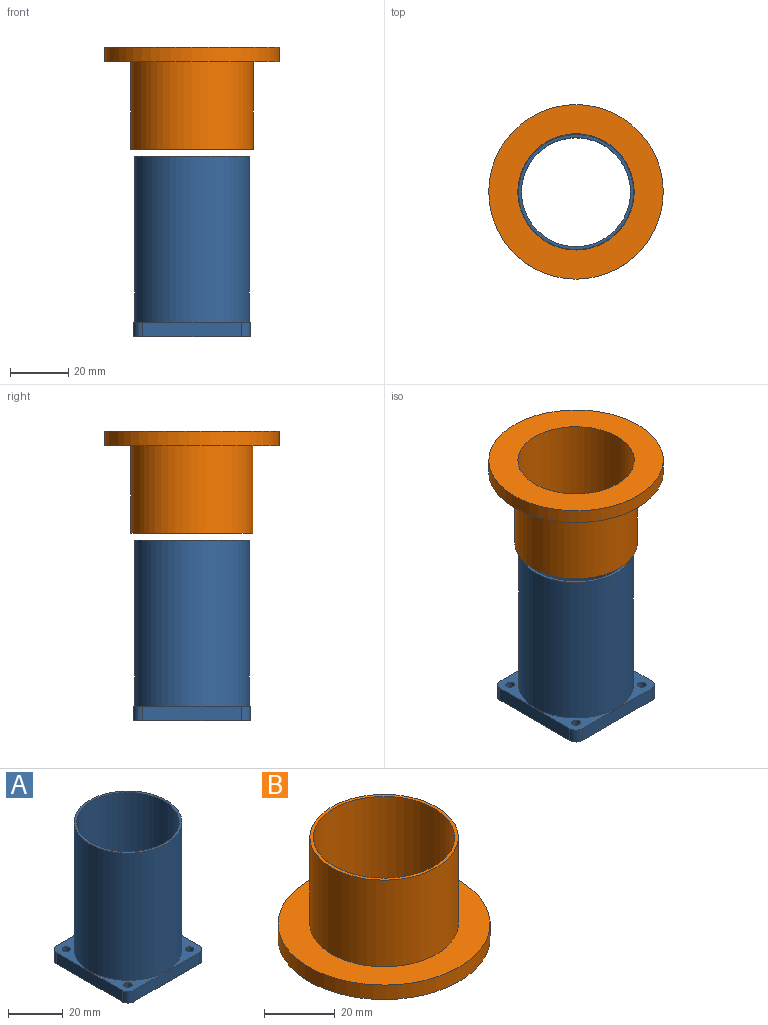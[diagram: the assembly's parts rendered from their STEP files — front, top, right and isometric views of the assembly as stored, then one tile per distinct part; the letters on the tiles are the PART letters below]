
ASSEMBLY  parts=2 mates=1
PART A: 17 faces, bbox 40x40x62 mm
  f0: plane 34x5mm, normal (0,-1,0), area 170mm2, adj f1,f12,f13,f14
  f1: cylinder r=3mm len=5mm, axis (0,0,-1), area 23.6mm2, adj f0,f2,f13,f14
  f2: plane 34x5mm, normal (1,0,0), area 170mm2, adj f1,f3,f13,f14
  f3: cylinder r=3mm len=5mm, axis (0,0,-1), area 23.6mm2, adj f2,f4,f13,f14
  f4: plane 34x5mm, normal (0,1,0), area 170mm2, adj f3,f5,f13,f14
  f5: cylinder r=3mm len=5mm, axis (0,0,-1), area 23.6mm2, adj f4,f6,f13,f14
  f6: plane 34x5mm, normal (-1,0,0), area 170mm2, adj f5,f12,f13,f14
  f7: cylinder r=18.75mm len=62mm, axis (0,0,-1), area 7304.2mm2, adj f14,f16
  f8: cylinder r=1.5mm len=5mm, axis (0,0,-1), area 47.1mm2, adj f13,f14
  f9: cylinder r=1.5mm len=5mm, axis (0,0,-1), area 47.1mm2, adj f13,f14
  f10: cylinder r=1.5mm len=5mm, axis (0,0,-1), area 47.1mm2, adj f13,f14
  f11: cylinder r=1.5mm len=5mm, axis (0,0,-1), area 47.1mm2, adj f13,f14
  f12: cylinder r=3mm len=5mm, axis (0,0,-1), area 23.6mm2, adj f0,f6,f13,f14
  f13: plane 40x40mm, normal (0,0,1), area 338.6mm2, adj f0,f1,f2,f3,f4,f5,f6,f8
  f14: plane 40x40mm, normal (0,0,-1), area 459.5mm2, adj f0,f1,f2,f3,f4,f5,f6,f7
  f15: cylinder r=19.75mm len=57mm, axis (0,0,-1), area 7073.3mm2, adj f13,f16
  f16: plane 39.5x39.5mm, normal (0,0,1), area 121mm2, adj f7,f15
PART B: 6 faces, bbox 60x60x35 mm
  f0: cylinder r=20mm len=40mm, axis (0,0,-1), area 4398.2mm2, adj f3,f5
  f1: cylinder r=30mm len=60mm, axis (0,0,-1), area 942.5mm2, adj f2,f3
  f2: plane 60x60mm, normal (0,0,1), area 1442mm2, adj f1,f4
  f3: plane 60x60mm, normal (0,0,-1), area 1570.8mm2, adj f0,f1
  f4: cylinder r=21mm len=42mm, axis (0,0,-1), area 3958.4mm2, adj f2,f5
  f5: plane 42x42mm, normal (0,0,1), area 128.8mm2, adj f0,f4
PLACE A t=(-1.8,10.21,-10.96)mm
PLACE B rot(axis=(-0.71,0.71,0),180deg) t=(-1.8,10.21,88.54)mm
MATE slider B.f0 <-> A.f7  axis (0,0,1) through (-1.8,10.21,53.54)mm
